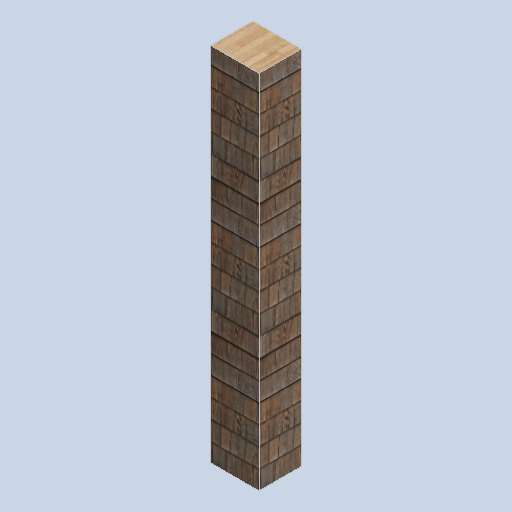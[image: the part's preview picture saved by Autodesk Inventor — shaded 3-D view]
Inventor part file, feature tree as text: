
AUTODESK INVENTOR PART (.ipt)
format: ipt  version: 2024.2 (Build 282272000, 272)  size: 178,688 bytes
history: native  units: in
note: dims shown in document units (in); Inventor stores cm internally (conversion verified against a paired STEP export)
features: other x3, sketch x1
ambient origin geometry x8: Origin, YZ Plane, XZ Plane, XY Plane, X Axis, Y Axis, Z Axis, Center Point
bodies: Solid1 (feature_tree)
feature tree (4):
  other  "support_column_02_MIR.ipt"
  other  "Solid1::support_column_02_MIR.ipt"
  other  "TaggingFeature1"
  sketch  "Sketch1"  dims[d0=0.3937in]
